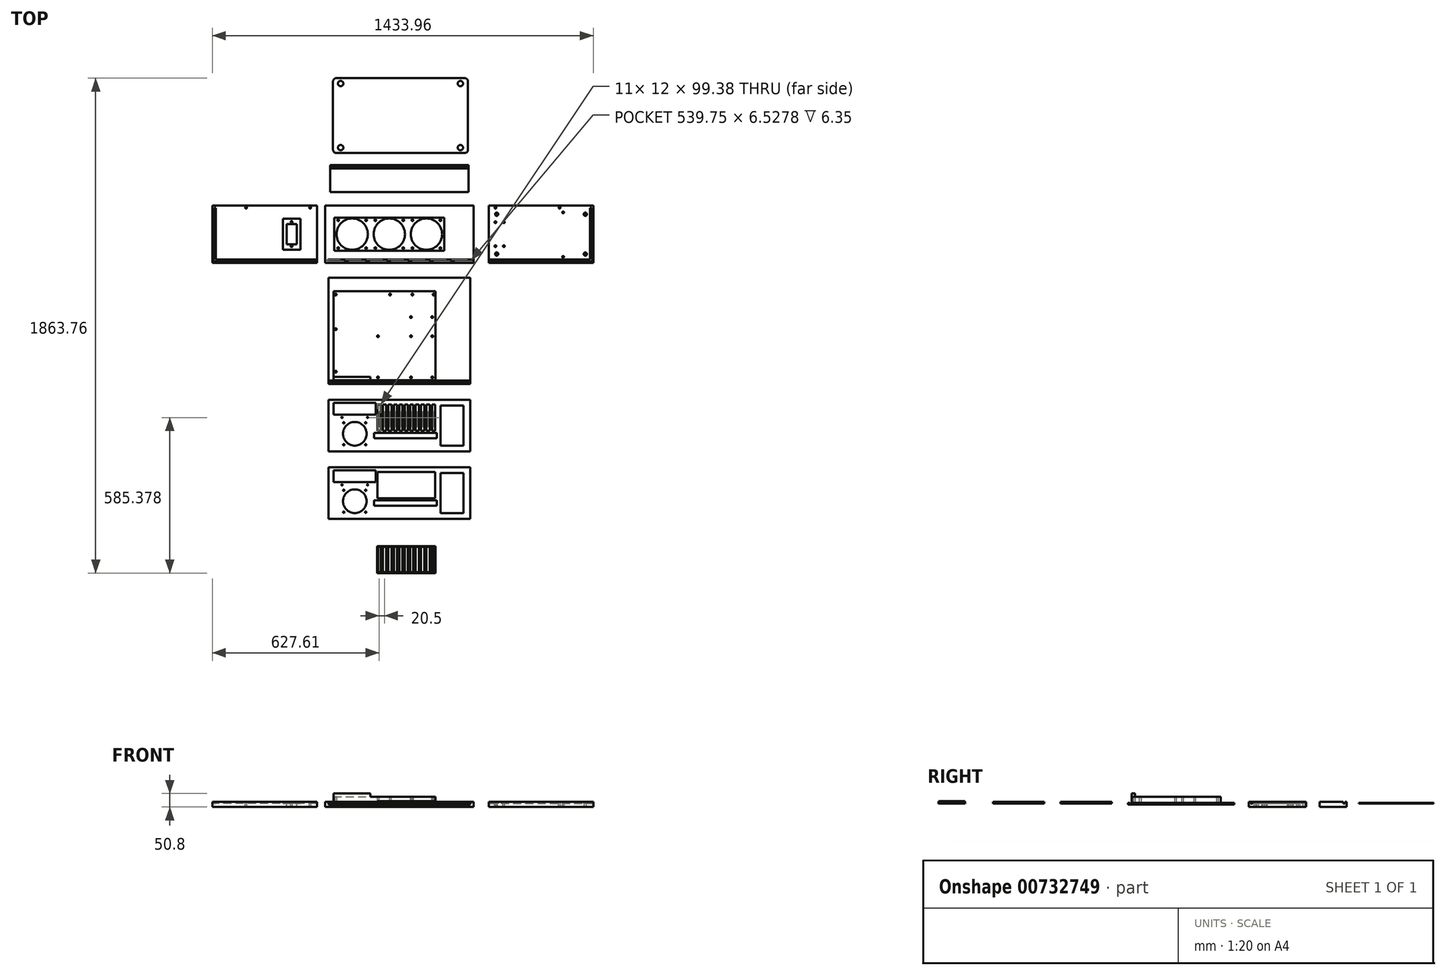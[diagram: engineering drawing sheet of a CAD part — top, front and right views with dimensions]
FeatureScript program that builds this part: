
annotation { "Feature Type Name" : "Feature", "Feature Type Description" : "" }
export const myFeature = defineFeature(function(context is Context, id is Id, definition is map)
    precondition{}
    {
        {
            var Q0;
            Q0=qCreatedBy(makeId("Top.planeOp"),FACE);
            var sketch = newSketch(context, id + "F0", { "sketchPlane" : qUnion([Q0])});
            skLineSegment(sketch, "E0.bottom", {"start": v(279.4, -107.95) * mm, "end": v(-279.4, -107.95) * mm});
            skLineSegment(sketch, "E0.top", {"start": v(279.4, 107.95) * mm, "end": v(-279.4, 107.95) * mm});
            skLineSegment(sketch, "E0.left", {"start": v(279.4, -107.95) * mm, "end": v(279.4, 107.95) * mm});
            skLineSegment(sketch, "E0.right", {"start": v(-279.4, -107.95) * mm, "end": v(-279.4, 107.95) * mm});
            skPoint(sketch, "E0.middle", {"position": v(0, 0) * mm});
            skLineSegment(sketch, "E1.bottom", {"start": v(269.88, -101.6) * mm, "end": v(-269.88, -101.6) * mm});
            skLineSegment(sketch, "E1.top", {"start": v(269.88, -95.07) * mm, "end": v(-269.88, -95.07) * mm});
            skLineSegment(sketch, "E1.left", {"start": v(269.88, -101.6) * mm, "end": v(269.88, -95.07) * mm});
            skLineSegment(sketch, "E1.right", {"start": v(-269.88, -101.6) * mm, "end": v(-269.88, -95.07) * mm});
            skPoint(sketch, "E1.middle", {"position": v(0, -98.34) * mm});
            skCircle(sketch, "E2", {"center": v(101.6, 0) * mm, "radius": 59 * mm});
            skCircle(sketch, "E3", {"center": v(-177.8, 0) * mm, "radius": 59 * mm});
            skCircle(sketch, "E4", {"center": v(-38.1, 0) * mm, "radius": 59 * mm});
            skCircle(sketch, "E5", {"center": v(-230.3, 52.5) * mm, "radius": 3.19 * mm});
            skCircle(sketch, "E6", {"center": v(-230.3, -52.5) * mm, "radius": 3.19 * mm});
            skCircle(sketch, "E7", {"center": v(-125.3, -52.5) * mm, "radius": 3.19 * mm});
            skCircle(sketch, "E8", {"center": v(-125.3, 52.5) * mm, "radius": 3.19 * mm});
            skCircle(sketch, "E9", {"center": v(-90.6, 52.5) * mm, "radius": 3.19 * mm});
            skCircle(sketch, "E10", {"center": v(14.4, 52.5) * mm, "radius": 3.19 * mm});
            skCircle(sketch, "E11", {"center": v(-90.6, -52.5) * mm, "radius": 3.19 * mm});
            skCircle(sketch, "E12", {"center": v(14.4, -52.5) * mm, "radius": 3.19 * mm});
            skCircle(sketch, "E13", {"center": v(49.1, -52.5) * mm, "radius": 3.19 * mm});
            skCircle(sketch, "E14", {"center": v(49.1, 52.5) * mm, "radius": 3.19 * mm});
            skCircle(sketch, "E15", {"center": v(154.1, 52.5) * mm, "radius": 3.19 * mm});
            skCircle(sketch, "E16", {"center": v(154.1, -52.5) * mm, "radius": 3.19 * mm});
            skLineSegment(sketch, "E17.bottom", {"start": v(169.07, -62.5) * mm, "end": v(-245.27, -62.5) * mm});
            skLineSegment(sketch, "E17.top", {"start": v(169.07, 62.5) * mm, "end": v(-245.27, 62.5) * mm});
            skLineSegment(sketch, "E17.left", {"start": v(169.07, -62.5) * mm, "end": v(169.07, 62.5) * mm});
            skLineSegment(sketch, "E17.right", {"start": v(-245.27, -62.5) * mm, "end": v(-245.27, 62.5) * mm});
            skSolve(sketch);
        }
        {
            var Q0;
            Q0=makeQuery(id+"F0.imprint","IMPRINT",FACE,{"disambiguationData":[TD([[makeQuery(id+"F0.imprint","IMPRINT",EDGE,{"derivedFrom":sQuery(id+"F0.wireOp",EDGE,"E1.bottom")}),-1.0]])]});
            var Q1;
            Q1=makeQuery(id+"F0.imprint","IMPRINT",FACE,{"disambiguationData":[TD([[makeQuery(id+"F0.imprint","IMPRINT",EDGE,{"derivedFrom":sQuery(id+"F0.wireOp",EDGE,"E0.bottom")}),-1.0]])]});
            var Q2;
            Q2=makeQuery(id+"F0.imprint","IMPRINT",FACE,{"disambiguationData":[TD([[makeQuery(id+"F0.imprint","IMPRINT",EDGE,{"derivedFrom":sQuery(id+"F0.wireOp",EDGE,"E2")}),-1.0]])]});
            extrude(context, id + "F1", {"entities" : qUnion([Q0, Q1, Q2]), "oppositeDirection" : true, "depth" : 12.7 * mm, "offsetDistance" : 25.4 * mm});
        }
        {
            var Q0;
            Q0=makeQuery(id+"F0.imprint","IMPRINT",FACE,{"disambiguationData":[TD([[makeQuery(id+"F0.imprint","IMPRINT",EDGE,{"derivedFrom":sQuery(id+"F0.wireOp",EDGE,"E0.bottom")}),-1.0]])]});
            extrude(context, id + "F2", {"entities" : qUnion([Q0]), "operationType" : NewBodyOperationType.ADD, "depth" : 6.35 * mm, "offsetDistance" : 25.4 * mm});
        }
        {
            var Q0;
            Q0=qCreatedBy(makeId("Top.planeOp"),FACE);
            var sketch = newSketch(context, id + "F3", { "sketchPlane" : qUnion([Q0])});
            skPoint(sketch, "E18.0", {"position": v(269.88, -95.07) * mm});
            skPoint(sketch, "E18.1", {"position": v(269.88, -101.6) * mm});
            skPoint(sketch, "E18.2", {"position": v(279.4, -107.95) * mm});
            skPoint(sketch, "E18.3", {"position": v(279.4, 107.95) * mm});
            skLineSegment(sketch, "E19.bottom", {"start": v(336.1, -107.95) * mm, "end": v(729.8, -107.95) * mm});
            skLineSegment(sketch, "E19.top", {"start": v(336.1, 107.95) * mm, "end": v(729.8, 107.95) * mm});
            skLineSegment(sketch, "E19.left", {"start": v(336.1, -107.95) * mm, "end": v(336.1, 107.95) * mm});
            skLineSegment(sketch, "E19.right", {"start": v(729.8, -107.95) * mm, "end": v(729.8, 107.95) * mm});
            skPoint(sketch, "E19.middle", {"position": v(532.95, 0) * mm});
            skLineSegment(sketch, "E20.bottom", {"start": v(332.93, -95.07) * mm, "end": v(732.98, -95.07) * mm});
            skLineSegment(sketch, "E20.top", {"start": v(332.93, -101.6) * mm, "end": v(732.98, -101.6) * mm});
            skLineSegment(sketch, "E20.left", {"start": v(332.93, -95.07) * mm, "end": v(332.93, -101.6) * mm});
            skLineSegment(sketch, "E20.right", {"start": v(732.98, -95.07) * mm, "end": v(732.98, -101.6) * mm});
            skLineSegment(sketch, "E21.bottom", {"start": v(723.45, -97.9) * mm, "end": v(717.08, -97.9) * mm});
            skLineSegment(sketch, "E21.top", {"start": v(723.45, 98.42) * mm, "end": v(717.08, 98.42) * mm});
            skLineSegment(sketch, "E21.left", {"start": v(723.45, -97.9) * mm, "end": v(723.45, 98.42) * mm});
            skLineSegment(sketch, "E21.right", {"start": v(717.08, -97.9) * mm, "end": v(717.08, 98.42) * mm});
            skCircle(sketch, "E22", {"center": v(366.1, 74.95) * mm, "radius": 3.3 * mm});
            skCircle(sketch, "E23", {"center": v(366.1, -74.95) * mm, "radius": 3.3 * mm});
            skCircle(sketch, "E24", {"center": v(699.8, -74.95) * mm, "radius": 3.3 * mm});
            skCircle(sketch, "E25", {"center": v(699.8, 74.95) * mm, "radius": 3.3 * mm});
            skCircle(sketch, "E26", {"center": v(366.1, 74.95) * mm, "radius": 6 * mm});
            skCircle(sketch, "E27", {"center": v(366.1, -74.95) * mm, "radius": 6 * mm});
            skCircle(sketch, "E28", {"center": v(699.8, 74.95) * mm, "radius": 6 * mm});
            skCircle(sketch, "E29", {"center": v(699.8, -74.95) * mm, "radius": 6 * mm});
            skPoint(sketch, "E30", {"position": v(628.2, -20.34) * mm});
            skCircle(sketch, "E31", {"center": v(602.8, 99.95) * mm, "radius": 3.3 * mm});
            skCircle(sketch, "E32", {"center": v(361.5, 99.95) * mm, "radius": 3.3 * mm});
            skPoint(sketch, "E33.centerSnap0", {"position": v(336.1, 0) * mm});
            skCircle(sketch, "E34", {"center": v(616.08, 81.95) * mm, "radius": 3.3 * mm});
            skCircle(sketch, "E35", {"center": v(616.08, -85.4) * mm, "radius": 3.3 * mm});
            skLineSegment(sketch, "E36.bottom", {"start": v(393.3, -45.09) * mm, "end": v(361.5, -45.09) * mm});
            skLineSegment(sketch, "E36.top", {"start": v(393.3, 45.08) * mm, "end": v(361.5, 45.08) * mm});
            skLineSegment(sketch, "E36.left", {"start": v(393.3, -45.09) * mm, "end": v(393.3, 45.08) * mm});
            skLineSegment(sketch, "E36.right", {"start": v(361.5, -45.09) * mm, "end": v(361.5, 45.08) * mm});
            skPoint(sketch, "E36.middle", {"position": v(377.4, 0) * mm});
            skCircle(sketch, "E37", {"center": v(361.5, 45.08) * mm, "radius": 3.3 * mm});
            skCircle(sketch, "E38", {"center": v(393.3, 45.08) * mm, "radius": 3.3 * mm});
            skCircle(sketch, "E39", {"center": v(361.5, -45.09) * mm, "radius": 3.3 * mm});
            skCircle(sketch, "E40", {"center": v(393.3, -45.09) * mm, "radius": 3.3 * mm});
            skSolve(sketch);
        }
        {
            var Q0;
            {var subQ0=sQuery(id+"F3.wireOp",EDGE,"E19.left");var subQ1=sQuery(id+"F3.wireOp",EDGE,"E19.top");var subQ2=makeQuery(id+"F3.imprint","INTERSECT",VERTEX,{"derivedFrom":[subQ1,subQ0]});Q0=makeQuery(id+"F3.imprint","IMPRINT",FACE,{"disambiguationData":[TD([[makeQuery(id+"F3.imprint","IMPRINT",EDGE,{"disambiguationData":[TD([[subQ2,-1.0]])],"derivedFrom":subQ1}),-1.0]])]});}
            var Q1;
            {var subQ0=sQuery(id+"F3.wireOp",EDGE,"E21.right");var subQ1=sQuery(id+"F3.wireOp",EDGE,"E19.top");var subQ2=makeQuery(id+"F3.imprint","INTERSECT",VERTEX,{"derivedFrom":[subQ1,subQ0]});Q1=makeQuery(id+"F3.imprint","IMPRINT",FACE,{"disambiguationData":[TD([[makeQuery(id+"F3.imprint","IMPRINT",EDGE,{"disambiguationData":[TD([[subQ2,-1.0]])],"derivedFrom":subQ1}),-1.0]])]});}
            var Q2;
            {var subQ0=sQuery(id+"F3.wireOp",EDGE,"E19.right");var subQ1=sQuery(id+"F3.wireOp",EDGE,"E19.top");var subQ2=makeQuery(id+"F3.imprint","INTERSECT",VERTEX,{"derivedFrom":[subQ1,subQ0]});Q2=makeQuery(id+"F3.imprint","IMPRINT",FACE,{"disambiguationData":[TD([[makeQuery(id+"F3.imprint","IMPRINT",EDGE,{"disambiguationData":[TD([[subQ2,1.0]])],"derivedFrom":subQ1}),-1.0]])]});}
            var Q3;
            {var subQ6=sQuery(id+"F3.wireOp",EDGE,"E21.bottom");Q3=makeQuery(id+"F3.imprint","IMPRINT",FACE,{"disambiguationData":[TD([[makeQuery(id+"F3.imprint","IMPRINT",EDGE,{"derivedFrom":subQ6}),1.0]])]});}
            var Q4;
            {var subQ0=sQuery(id+"F3.wireOp",EDGE,"E19.bottom");Q4=makeQuery(id+"F3.imprint","IMPRINT",FACE,{"disambiguationData":[TD([[makeQuery(id+"F3.imprint","IMPRINT",EDGE,{"derivedFrom":subQ0}),1.0]])]});}
            var Q5;
            {var subQ5=sQuery(id+"F3.wireOp",EDGE,"E21.bottom");Q5=makeQuery(id+"F3.imprint","IMPRINT",FACE,{"disambiguationData":[TD([[makeQuery(id+"F3.imprint","IMPRINT",EDGE,{"derivedFrom":subQ5}),-1.0]])]});}
            var Q6;
            {var subQ5=sQuery(id+"F3.wireOp",EDGE,"E21.top");Q6=makeQuery(id+"F3.imprint","IMPRINT",FACE,{"disambiguationData":[TD([[makeQuery(id+"F3.imprint","IMPRINT",EDGE,{"derivedFrom":subQ5}),1.0]])]});}
            var Q7;
            Q7=makeQuery(id+"F3.imprint","IMPRINT",FACE,{"disambiguationData":[TD([[makeQuery(id+"F3.imprint","IMPRINT",EDGE,{"derivedFrom":sQuery(id+"F3.wireOp",EDGE,"E22")}),-1.0]])]});
            var Q8;
            Q8=makeQuery(id+"F3.imprint","IMPRINT",FACE,{"disambiguationData":[TD([[makeQuery(id+"F3.imprint","IMPRINT",EDGE,{"derivedFrom":sQuery(id+"F3.wireOp",EDGE,"E23")}),-1.0]])]});
            var Q9;
            Q9=makeQuery(id+"F3.imprint","IMPRINT",FACE,{"disambiguationData":[TD([[makeQuery(id+"F3.imprint","IMPRINT",EDGE,{"derivedFrom":sQuery(id+"F3.wireOp",EDGE,"E24")}),-1.0]])]});
            var Q10;
            Q10=makeQuery(id+"F3.imprint","IMPRINT",FACE,{"disambiguationData":[TD([[makeQuery(id+"F3.imprint","IMPRINT",EDGE,{"derivedFrom":sQuery(id+"F3.wireOp",EDGE,"E25")}),-1.0]])]});
            var Q11;
            {var subQ0=sQuery(id+"F3.wireOp",EDGE,"E36.top");var subQ1=sQuery(id+"F3.wireOp",EDGE,"oCOWhfAx-kF6R-myvc-yPfL-ItVIfWdrZVwj");var subQ2=makeQuery(id+"F3.imprint","INTERSECT",VERTEX,{"derivedFrom":[subQ1,subQ0]});Q11=makeQuery(id+"F3.imprint","IMPRINT",FACE,{"disambiguationData":[TD([[makeQuery(id+"F3.imprint","IMPRINT",EDGE,{"disambiguationData":[TD([[subQ2,-1.0]])],"derivedFrom":subQ1}),-1.0]])]});}
            var Q12;
            {var subQ5=sQuery(id+"F3.wireOp",EDGE,"E36.top");var subQ6=sQuery(id+"F3.wireOp",EDGE,"oCOWhfAx-kF6R-myvc-yPfL-ItVIfWdrZVwj");var subQ7=makeQuery(id+"F3.imprint","INTERSECT",VERTEX,{"derivedFrom":[subQ6,subQ5]});Q12=makeQuery(id+"F3.imprint","IMPRINT",FACE,{"disambiguationData":[TD([[makeQuery(id+"F3.imprint","IMPRINT",EDGE,{"disambiguationData":[TD([[subQ7,-1.0]])],"derivedFrom":subQ6}),1.0]])]});}
            var Q13;
            {var subQ5=sQuery(id+"F3.wireOp",EDGE,"E40");var subQ10=sQuery(id+"F3.wireOp",EDGE,"E36.bottom");var subQ11=makeQuery(id+"F3.imprint","INTERSECT",VERTEX,{"derivedFrom":[subQ10,subQ5]});Q13=makeQuery(id+"F3.imprint","IMPRINT",FACE,{"disambiguationData":[TD([[makeQuery(id+"F3.imprint","IMPRINT",EDGE,{"disambiguationData":[TD([[subQ11,-1.0]])],"derivedFrom":subQ10}),-1.0]])]});}
            extrude(context, id + "F4", {"entities" : qUnion([Q0, Q1, Q2, Q3, Q4, Q5, Q6, Q7, Q8, Q9, Q10, Q11, Q12, Q13]), "oppositeDirection" : true, "depth" : 12.7 * mm, "offsetDistance" : 25.4 * mm});
        }
        {
            var Q0;
            {var subQ0=sQuery(id+"F3.wireOp",EDGE,"E19.left");var subQ1=sQuery(id+"F3.wireOp",EDGE,"E19.top");var subQ2=makeQuery(id+"F3.imprint","INTERSECT",VERTEX,{"derivedFrom":[subQ1,subQ0]});Q0=makeQuery(id+"F3.imprint","IMPRINT",FACE,{"disambiguationData":[TD([[makeQuery(id+"F3.imprint","IMPRINT",EDGE,{"disambiguationData":[TD([[subQ2,-1.0]])],"derivedFrom":subQ1}),-1.0]])]});}
            var Q1;
            {var subQ0=sQuery(id+"F3.wireOp",EDGE,"E19.right");var subQ1=sQuery(id+"F3.wireOp",EDGE,"E19.top");var subQ2=makeQuery(id+"F3.imprint","INTERSECT",VERTEX,{"derivedFrom":[subQ1,subQ0]});Q1=makeQuery(id+"F3.imprint","IMPRINT",FACE,{"disambiguationData":[TD([[makeQuery(id+"F3.imprint","IMPRINT",EDGE,{"disambiguationData":[TD([[subQ2,1.0]])],"derivedFrom":subQ1}),-1.0]])]});}
            var Q2;
            {var subQ0=sQuery(id+"F3.wireOp",EDGE,"E19.bottom");Q2=makeQuery(id+"F3.imprint","IMPRINT",FACE,{"disambiguationData":[TD([[makeQuery(id+"F3.imprint","IMPRINT",EDGE,{"derivedFrom":subQ0}),1.0]])]});}
            var Q3;
            {var subQ0=sQuery(id+"F3.wireOp",EDGE,"E36.top");var subQ1=sQuery(id+"F3.wireOp",EDGE,"oCOWhfAx-kF6R-myvc-yPfL-ItVIfWdrZVwj");var subQ2=makeQuery(id+"F3.imprint","INTERSECT",VERTEX,{"derivedFrom":[subQ1,subQ0]});Q3=makeQuery(id+"F3.imprint","IMPRINT",FACE,{"disambiguationData":[TD([[makeQuery(id+"F3.imprint","IMPRINT",EDGE,{"disambiguationData":[TD([[subQ2,-1.0]])],"derivedFrom":subQ1}),-1.0]])]});}
            var Q4;
            {var subQ5=sQuery(id+"F3.wireOp",EDGE,"E36.top");var subQ6=sQuery(id+"F3.wireOp",EDGE,"oCOWhfAx-kF6R-myvc-yPfL-ItVIfWdrZVwj");var subQ7=makeQuery(id+"F3.imprint","INTERSECT",VERTEX,{"derivedFrom":[subQ6,subQ5]});Q4=makeQuery(id+"F3.imprint","IMPRINT",FACE,{"disambiguationData":[TD([[makeQuery(id+"F3.imprint","IMPRINT",EDGE,{"disambiguationData":[TD([[subQ7,-1.0]])],"derivedFrom":subQ6}),1.0]])]});}
            var Q5;
            {var subQ5=sQuery(id+"F3.wireOp",EDGE,"E40");var subQ10=sQuery(id+"F3.wireOp",EDGE,"E36.bottom");var subQ11=makeQuery(id+"F3.imprint","INTERSECT",VERTEX,{"derivedFrom":[subQ10,subQ5]});Q5=makeQuery(id+"F3.imprint","IMPRINT",FACE,{"disambiguationData":[TD([[makeQuery(id+"F3.imprint","IMPRINT",EDGE,{"disambiguationData":[TD([[subQ11,-1.0]])],"derivedFrom":subQ10}),-1.0]])]});}
            extrude(context, id + "F5", {"entities" : qUnion([Q0, Q1, Q2, Q3, Q4, Q5]), "operationType" : NewBodyOperationType.ADD, "depth" : 6.35 * mm, "offsetDistance" : 25.4 * mm});
        }
        {
            var Q0;
            Q0=qCreatedBy(makeId("Top.planeOp"),FACE);
            var sketch = newSketch(context, id + "F6", { "sketchPlane" : qUnion([Q0])});
            skPoint(sketch, "E41.0", {"position": v(-279.4, 107.95) * mm});
            skPoint(sketch, "E41.1", {"position": v(-279.4, -107.95) * mm});
            skPoint(sketch, "E41.2", {"position": v(-269.88, -95.07) * mm});
            skPoint(sketch, "E41.3", {"position": v(-269.88, -101.6) * mm});
            skLineSegment(sketch, "E42.bottom", {"start": v(-310.46, 107.95) * mm, "end": v(-704.16, 107.95) * mm});
            skLineSegment(sketch, "E42.top", {"start": v(-310.46, -107.95) * mm, "end": v(-704.16, -107.95) * mm});
            skLineSegment(sketch, "E42.left", {"start": v(-310.46, 107.95) * mm, "end": v(-310.46, -107.95) * mm});
            skLineSegment(sketch, "E42.right", {"start": v(-704.16, 107.95) * mm, "end": v(-704.16, -107.95) * mm});
            skLineSegment(sketch, "E43.bottom", {"start": v(-307.28, -95.07) * mm, "end": v(-707.33, -95.07) * mm});
            skLineSegment(sketch, "E43.top", {"start": v(-307.28, -101.6) * mm, "end": v(-707.33, -101.6) * mm});
            skLineSegment(sketch, "E43.left", {"start": v(-307.28, -95.07) * mm, "end": v(-307.28, -101.6) * mm});
            skLineSegment(sketch, "E43.right", {"start": v(-707.33, -95.07) * mm, "end": v(-707.33, -101.6) * mm});
            skLineSegment(sketch, "E44.bottom", {"start": v(-386.66, -38.1) * mm, "end": v(-424.76, -38.1) * mm});
            skLineSegment(sketch, "E44.top", {"start": v(-386.66, 38.1) * mm, "end": v(-424.76, 38.1) * mm});
            skLineSegment(sketch, "E44.left", {"start": v(-386.66, -38.1) * mm, "end": v(-386.66, 38.1) * mm});
            skLineSegment(sketch, "E44.right", {"start": v(-424.76, -38.1) * mm, "end": v(-424.76, 38.1) * mm});
            skPoint(sketch, "E44.middle", {"position": v(-405.7, 0) * mm});
            skLineSegment(sketch, "E45.bottom", {"start": v(-697.8, 98.42) * mm, "end": v(-691.43, 98.42) * mm});
            skLineSegment(sketch, "E45.top", {"start": v(-697.8, -99.05) * mm, "end": v(-691.43, -99.05) * mm});
            skLineSegment(sketch, "E45.left", {"start": v(-697.8, 98.42) * mm, "end": v(-697.8, -99.05) * mm});
            skLineSegment(sketch, "E45.right", {"start": v(-691.43, 98.42) * mm, "end": v(-691.43, -99.05) * mm});
            skPoint(sketch, "E46.0", {"position": v(361.5, 99.95) * mm});
            skCircle(sketch, "E47", {"center": v(-335.86, 99.95) * mm, "radius": 3.3 * mm});
            skCircle(sketch, "E48", {"center": v(-577.16, 99.95) * mm, "radius": 3.3 * mm});
            skCircle(sketch, "E49", {"center": v(-405.7, 45.6) * mm, "radius": 3.3 * mm});
            skCircle(sketch, "E50", {"center": v(-405.7, -45.6) * mm, "radius": 3.3 * mm});
            skLineSegment(sketch, "E51.bottom", {"start": v(-438.73, 58.42) * mm, "end": v(-372.69, 58.42) * mm});
            skLineSegment(sketch, "E51.top", {"start": v(-438.73, -58.42) * mm, "end": v(-372.69, -58.42) * mm});
            skLineSegment(sketch, "E51.left", {"start": v(-438.73, 58.42) * mm, "end": v(-438.73, -58.42) * mm});
            skLineSegment(sketch, "E51.right", {"start": v(-372.69, 58.42) * mm, "end": v(-372.69, -58.42) * mm});
            skSolve(sketch);
        }
        {
            var Q0;
            Q0=makeQuery(id+"F6.imprint","IMPRINT",FACE,{"disambiguationData":[TD([[makeQuery(id+"F6.imprint","IMPRINT",EDGE,{"derivedFrom":sQuery(id+"F6.wireOp",EDGE,"E44.bottom")}),1.0]])]});
            var Q1;
            {var subQ0=sQuery(id+"F6.wireOp",EDGE,"E42.top");Q1=makeQuery(id+"F6.imprint","IMPRINT",FACE,{"disambiguationData":[TD([[makeQuery(id+"F6.imprint","IMPRINT",EDGE,{"derivedFrom":subQ0}),-1.0]])]});}
            var Q2;
            {var subQ12=sQuery(id+"F6.wireOp",EDGE,"E45.top");Q2=makeQuery(id+"F6.imprint","IMPRINT",FACE,{"disambiguationData":[TD([[makeQuery(id+"F6.imprint","IMPRINT",EDGE,{"derivedFrom":subQ12}),-1.0]])]});}
            var Q3;
            {var subQ0=sQuery(id+"F6.wireOp",EDGE,"E42.right");var subQ1=sQuery(id+"F6.wireOp",EDGE,"E42.bottom");var subQ2=makeQuery(id+"F6.imprint","INTERSECT",VERTEX,{"derivedFrom":[subQ1,subQ0]});Q3=makeQuery(id+"F6.imprint","IMPRINT",FACE,{"disambiguationData":[TD([[makeQuery(id+"F6.imprint","IMPRINT",EDGE,{"disambiguationData":[TD([[subQ2,1.0]])],"derivedFrom":subQ1}),1.0]])]});}
            var Q4;
            {var subQ0=sQuery(id+"F6.wireOp",EDGE,"E45.right");var subQ1=sQuery(id+"F6.wireOp",EDGE,"E42.bottom");var subQ2=makeQuery(id+"F6.imprint","INTERSECT",VERTEX,{"derivedFrom":[subQ1,subQ0]});Q4=makeQuery(id+"F6.imprint","IMPRINT",FACE,{"disambiguationData":[TD([[makeQuery(id+"F6.imprint","IMPRINT",EDGE,{"disambiguationData":[TD([[subQ2,-1.0]])],"derivedFrom":subQ1}),1.0]])]});}
            var Q5;
            {var subQ5=sQuery(id+"F6.wireOp",EDGE,"E45.top");Q5=makeQuery(id+"F6.imprint","IMPRINT",FACE,{"disambiguationData":[TD([[makeQuery(id+"F6.imprint","IMPRINT",EDGE,{"derivedFrom":subQ5}),1.0]])]});}
            var Q6;
            {var subQ5=sQuery(id+"F6.wireOp",EDGE,"E45.bottom");Q6=makeQuery(id+"F6.imprint","IMPRINT",FACE,{"disambiguationData":[TD([[makeQuery(id+"F6.imprint","IMPRINT",EDGE,{"derivedFrom":subQ5}),-1.0]])]});}
            extrude(context, id + "F7", {"entities" : qUnion([Q0, Q1, Q2, Q3, Q4, Q5, Q6]), "oppositeDirection" : true, "depth" : 12.7 * mm, "offsetDistance" : 25.4 * mm});
        }
        {
            var Q0;
            Q0=makeQuery(id+"F6.imprint","IMPRINT",FACE,{"disambiguationData":[TD([[makeQuery(id+"F6.imprint","IMPRINT",EDGE,{"derivedFrom":sQuery(id+"F6.wireOp",EDGE,"E44.bottom")}),1.0]])]});
            var Q1;
            {var subQ0=sQuery(id+"F6.wireOp",EDGE,"E42.right");var subQ1=sQuery(id+"F6.wireOp",EDGE,"E42.bottom");var subQ2=makeQuery(id+"F6.imprint","INTERSECT",VERTEX,{"derivedFrom":[subQ1,subQ0]});Q1=makeQuery(id+"F6.imprint","IMPRINT",FACE,{"disambiguationData":[TD([[makeQuery(id+"F6.imprint","IMPRINT",EDGE,{"disambiguationData":[TD([[subQ2,1.0]])],"derivedFrom":subQ1}),1.0]])]});}
            var Q2;
            {var subQ0=sQuery(id+"F6.wireOp",EDGE,"E42.top");Q2=makeQuery(id+"F6.imprint","IMPRINT",FACE,{"disambiguationData":[TD([[makeQuery(id+"F6.imprint","IMPRINT",EDGE,{"derivedFrom":subQ0}),-1.0]])]});}
            extrude(context, id + "F8", {"entities" : qUnion([Q0, Q1, Q2]), "operationType" : NewBodyOperationType.ADD, "depth" : 6.35 * mm, "offsetDistance" : 25.4 * mm});
        }
        {
            var Q0;
            Q0=makeQuery(id+"F6.imprint","IMPRINT",FACE,{"disambiguationData":[TD([[makeQuery(id+"F6.imprint","IMPRINT",EDGE,{"derivedFrom":sQuery(id+"F6.wireOp",EDGE,"E44.bottom")}),1.0]])]});
            extrude(context, id + "F9", {"entities" : qUnion([Q0]), "operationType" : NewBodyOperationType.REMOVE, "depth" : 6.35 * mm, "offsetDistance" : 25.4 * mm});
        }
        {
            var Q0;
            Q0=qCreatedBy(makeId("Top.planeOp"),FACE);
            var sketch = newSketch(context, id + "F10", { "sketchPlane" : qUnion([Q0])});
            skLineSegment(sketch, "E52.bottom", {"start": v(136.35, -214.45) * mm, "end": v(136.35, -549.45) * mm});
            skLineSegment(sketch, "E52.top", {"start": v(-247.65, -214.45) * mm, "end": v(-247.65, -549.45) * mm});
            skLineSegment(sketch, "E52.left", {"start": v(136.35, -214.45) * mm, "end": v(-247.65, -214.45) * mm});
            skLineSegment(sketch, "E52.right", {"start": v(136.35, -549.45) * mm, "end": v(-247.65, -549.45) * mm});
            skLineSegment(sketch, "E53.bottom", {"start": v(-109.56, -549.45) * mm, "end": v(-109.56, -536.83) * mm});
            skLineSegment(sketch, "E53.top", {"start": v(-247.65, -549.45) * mm, "end": v(-247.65, -536.83) * mm});
            skLineSegment(sketch, "E53.left", {"start": v(-109.56, -549.45) * mm, "end": v(-247.65, -549.45) * mm});
            skLineSegment(sketch, "E53.right", {"start": v(-109.56, -536.83) * mm, "end": v(-247.65, -536.83) * mm});
            skCircle(sketch, "E54", {"center": v(-239.65, -517.45) * mm, "radius": 3.3 * mm});
            skCircle(sketch, "E55", {"center": v(-239.65, -357.45) * mm, "radius": 3.3 * mm});
            skCircle(sketch, "E56", {"center": v(-239.65, -227.45) * mm, "radius": 3.3 * mm});
            skCircle(sketch, "E57", {"center": v(-80.65, -539.45) * mm, "radius": 3.3 * mm});
            skCircle(sketch, "E58", {"center": v(-80.65, -384.45) * mm, "radius": 3.3 * mm});
            skCircle(sketch, "E59", {"center": v(43.35, -539.45) * mm, "radius": 3.3 * mm});
            skCircle(sketch, "E60", {"center": v(123.35, -539.45) * mm, "radius": 3.3 * mm});
            skCircle(sketch, "E61", {"center": v(123.35, -384.45) * mm, "radius": 3.3 * mm});
            skCircle(sketch, "E62", {"center": v(43.35, -384.45) * mm, "radius": 3.3 * mm});
            skCircle(sketch, "E63", {"center": v(123.35, -312.45) * mm, "radius": 3.3 * mm});
            skCircle(sketch, "E64", {"center": v(43.35, -312.45) * mm, "radius": 3.3 * mm});
            skCircle(sketch, "E65", {"center": v(128.85, -227.45) * mm, "radius": 3.3 * mm});
            skCircle(sketch, "E66", {"center": v(48.85, -227.45) * mm, "radius": 3.3 * mm});
            skCircle(sketch, "E67", {"center": v(-35.15, -227.45) * mm, "radius": 3.3 * mm});
            skSolve(sketch);
        }
        {
            var Q0;
            Q0=makeQuery(id+"F10.imprint","IMPRINT",FACE,{"disambiguationData":[TD([[makeQuery(id+"F10.imprint","IMPRINT",EDGE,{"derivedFrom":sQuery(id+"F10.wireOp",EDGE,"E52.bottom")}),-1.0]])]});
            var Q1;
            Q1=makeQuery(id+"F10.imprint","IMPRINT",FACE,{"disambiguationData":[TD([[makeQuery(id+"F10.imprint","IMPRINT",EDGE,{"derivedFrom":sQuery(id+"F10.wireOp",EDGE,"E53.bottom")}),1.0]])]});
            extrude(context, id + "F11", {"entities" : qUnion([Q0, Q1]), "depth" : 25.4 * mm, "offsetDistance" : 25.4 * mm});
        }
        {
            var Q0;
            Q0=makeQuery(id+"F10.imprint","IMPRINT",FACE,{"disambiguationData":[TD([[makeQuery(id+"F10.imprint","IMPRINT",EDGE,{"derivedFrom":sQuery(id+"F10.wireOp",EDGE,"E53.bottom")}),1.0]])]});
            extrude(context, id + "F12", {"entities" : qUnion([Q0]), "operationType" : NewBodyOperationType.ADD, "depth" : 38.1 * mm, "offsetDistance" : 25.4 * mm});
        }
        {
            var Q0;
            Q0=qCreatedBy(makeId("Top.planeOp"),FACE);
            var sketch = newSketch(context, id + "F13", { "sketchPlane" : qUnion([Q0])});
            skLineSegment(sketch, "E68.bottom", {"start": v(266.7, -563.67) * mm, "end": v(-266.7, -563.67) * mm});
            skLineSegment(sketch, "E68.top", {"start": v(266.7, -163.62) * mm, "end": v(-266.7, -163.62) * mm});
            skLineSegment(sketch, "E68.left", {"start": v(266.7, -563.67) * mm, "end": v(266.7, -163.62) * mm});
            skLineSegment(sketch, "E68.right", {"start": v(-266.7, -563.67) * mm, "end": v(-266.7, -163.62) * mm});
            skPoint(sketch, "E69.0", {"position": v(-279.4, -107.95) * mm});
            skPoint(sketch, "E69.1", {"position": v(279.4, -107.95) * mm});
            skLineSegment(sketch, "E70.bottom", {"start": v(269.88, -557.32) * mm, "end": v(-269.88, -557.32) * mm});
            skLineSegment(sketch, "E70.top", {"start": v(269.88, -550.8) * mm, "end": v(-269.88, -550.8) * mm});
            skLineSegment(sketch, "E70.left", {"start": v(269.88, -557.32) * mm, "end": v(269.88, -550.8) * mm});
            skLineSegment(sketch, "E70.right", {"start": v(-269.88, -557.32) * mm, "end": v(-269.88, -550.8) * mm});
            skCircle(sketch, "E71.0", {"center": v(-239.65, -227.45) * mm, "radius": 3.3 * mm});
            skCircle(sketch, "E71.1", {"center": v(-35.15, -227.45) * mm, "radius": 3.3 * mm});
            skCircle(sketch, "E71.2", {"center": v(48.85, -227.45) * mm, "radius": 3.3 * mm});
            skCircle(sketch, "E71.3", {"center": v(128.85, -227.45) * mm, "radius": 3.3 * mm});
            skCircle(sketch, "E71.4", {"center": v(43.35, -312.45) * mm, "radius": 3.3 * mm});
            skCircle(sketch, "E71.5", {"center": v(123.35, -312.45) * mm, "radius": 3.3 * mm});
            skCircle(sketch, "E71.6", {"center": v(43.35, -384.45) * mm, "radius": 3.3 * mm});
            skCircle(sketch, "E71.7", {"center": v(-80.65, -384.45) * mm, "radius": 3.3 * mm});
            skCircle(sketch, "E71.8", {"center": v(123.35, -384.45) * mm, "radius": 3.3 * mm});
            skCircle(sketch, "E71.9", {"center": v(-239.65, -357.45) * mm, "radius": 3.3 * mm});
            skCircle(sketch, "E71.10", {"center": v(-239.65, -517.45) * mm, "radius": 3.3 * mm});
            skCircle(sketch, "E71.11", {"center": v(-80.65, -539.45) * mm, "radius": 3.3 * mm});
            skCircle(sketch, "E71.12", {"center": v(43.35, -539.45) * mm, "radius": 3.3 * mm});
            skCircle(sketch, "E71.13", {"center": v(123.35, -539.45) * mm, "radius": 3.3 * mm});
            skSolve(sketch);
        }
        {
            var Q0;
            {var subQ0=sQuery(id+"F13.wireOp",EDGE,"E68.top");Q0=makeQuery(id+"F13.imprint","IMPRINT",FACE,{"disambiguationData":[TD([[makeQuery(id+"F13.imprint","IMPRINT",EDGE,{"derivedFrom":subQ0}),1.0]])]});}
            var Q1;
            {var subQ0=sQuery(id+"F13.wireOp",EDGE,"E70.bottom");var subQ1=sQuery(id+"F13.wireOp",EDGE,"E68.left");var subQ2=makeQuery(id+"F13.imprint","INTERSECT",VERTEX,{"derivedFrom":[subQ1,subQ0]});Q1=makeQuery(id+"F13.imprint","IMPRINT",FACE,{"disambiguationData":[TD([[makeQuery(id+"F13.imprint","IMPRINT",EDGE,{"disambiguationData":[TD([[subQ2,-1.0]])],"derivedFrom":subQ1}),1.0]])]});}
            var Q2;
            {var subQ0=sQuery(id+"F13.wireOp",EDGE,"E68.bottom");Q2=makeQuery(id+"F13.imprint","IMPRINT",FACE,{"disambiguationData":[TD([[makeQuery(id+"F13.imprint","IMPRINT",EDGE,{"derivedFrom":subQ0}),-1.0]])]});}
            extrude(context, id + "F14", {"entities" : qUnion([Q0, Q1, Q2]), "oppositeDirection" : true, "depth" : 3.2 * mm, "offsetDistance" : 25.4 * mm});
        }
        {
            var Q0;
            {var subQ0=sQuery(id+"F13.wireOp",EDGE,"E68.top");Q0=makeQuery(id+"F13.imprint","IMPRINT",FACE,{"disambiguationData":[TD([[makeQuery(id+"F13.imprint","IMPRINT",EDGE,{"derivedFrom":subQ0}),1.0]])]});}
            var Q1;
            {var subQ0=sQuery(id+"F13.wireOp",EDGE,"E68.bottom");Q1=makeQuery(id+"F13.imprint","IMPRINT",FACE,{"disambiguationData":[TD([[makeQuery(id+"F13.imprint","IMPRINT",EDGE,{"derivedFrom":subQ0}),-1.0]])]});}
            extrude(context, id + "F15", {"entities" : qUnion([Q0, Q1]), "operationType" : NewBodyOperationType.ADD, "depth" : 3.2 * mm, "offsetDistance" : 25.4 * mm});
        }
        {
            var Q0;
            Q0=qCreatedBy(makeId("Top.planeOp"),FACE);
            var sketch = newSketch(context, id + "F16", { "sketchPlane" : qUnion([Q0])});
            skPoint(sketch, "E72.0", {"position": v(-266.7, -563.67) * mm});
            skPoint(sketch, "E72.1", {"position": v(266.7, -563.67) * mm});
            skLineSegment(sketch, "E73.MirrorCS", {"start": v(-9.05, -641.22) * mm, "end": v(-21.05, -641.22) * mm});
            skLineSegment(sketch, "E74.MirrorCS", {"start": v(-29.55, -641.22) * mm, "end": v(-41.55, -641.22) * mm});
            skLineSegment(sketch, "E75.MirrorCS", {"start": v(113.95, -641.22) * mm, "end": v(101.95, -641.22) * mm});
            skLineSegment(sketch, "E76.MirrorCS", {"start": v(72.95, -641.22) * mm, "end": v(60.95, -641.22) * mm});
            skLineSegment(sketch, "E77.MirrorCS", {"start": v(134.45, -740.6) * mm, "end": v(122.45, -740.6) * mm});
            skLineSegment(sketch, "E78.MirrorCS", {"start": v(31.95, -641.22) * mm, "end": v(19.95, -641.22) * mm});
            skLineSegment(sketch, "E79.MirrorCS", {"start": v(-50.05, -641.22) * mm, "end": v(-62.05, -641.22) * mm});
            skLineSegment(sketch, "E80.MirrorCS", {"start": v(113.95, -740.6) * mm, "end": v(101.95, -740.6) * mm});
            skLineSegment(sketch, "E81.MirrorCS", {"start": v(11.45, -641.22) * mm, "end": v(-0.55, -641.22) * mm});
            skLineSegment(sketch, "E82.MirrorCS", {"start": v(-9.05, -740.6) * mm, "end": v(-21.05, -740.6) * mm});
            skLineSegment(sketch, "E83.MirrorCS", {"start": v(52.45, -740.6) * mm, "end": v(40.45, -740.6) * mm});
            skLineSegment(sketch, "E84.MirrorCS", {"start": v(-29.55, -740.6) * mm, "end": v(-41.55, -740.6) * mm});
            skLineSegment(sketch, "E85.MirrorCS", {"start": v(93.45, -641.22) * mm, "end": v(81.45, -641.22) * mm});
            skLineSegment(sketch, "E86.MirrorCS", {"start": v(93.45, -740.6) * mm, "end": v(81.45, -740.6) * mm});
            skLineSegment(sketch, "E87.MirrorCS", {"start": v(11.45, -740.6) * mm, "end": v(-0.55, -740.6) * mm});
            skLineSegment(sketch, "E88.MirrorCS", {"start": v(52.45, -641.22) * mm, "end": v(40.45, -641.22) * mm});
            skLineSegment(sketch, "E89.MirrorCS", {"start": v(-70.55, -740.6) * mm, "end": v(-82.55, -740.6) * mm});
            skLineSegment(sketch, "E90.MirrorCS", {"start": v(72.95, -740.6) * mm, "end": v(60.95, -740.6) * mm});
            skLineSegment(sketch, "E91.MirrorCS", {"start": v(134.45, -641.22) * mm, "end": v(122.45, -641.22) * mm});
            skLineSegment(sketch, "E92.MirrorCS", {"start": v(-50.05, -740.6) * mm, "end": v(-62.05, -740.6) * mm});
            skLineSegment(sketch, "E93.MirrorCS", {"start": v(31.95, -740.6) * mm, "end": v(19.95, -740.6) * mm});
            skLineSegment(sketch, "E94.MirrorCS", {"start": v(-70.55, -641.22) * mm, "end": v(-82.55, -641.22) * mm});
            skLineSegment(sketch, "E95.MirrorCS", {"start": v(-95.25, -748.22) * mm, "end": v(-95.25, -768.22) * mm});
            skLineSegment(sketch, "E96.MirrorCS", {"start": v(-95.25, -748.22) * mm, "end": v(140.8, -748.22) * mm});
            skLineSegment(sketch, "E97.MirrorCS", {"start": v(140.8, -748.22) * mm, "end": v(140.8, -768.22) * mm});
            skLineSegment(sketch, "E98.MirrorCS", {"start": v(134.45, -740.6) * mm, "end": v(134.45, -641.22) * mm});
            skLineSegment(sketch, "E99.MirrorCS", {"start": v(-50.05, -740.6) * mm, "end": v(-50.05, -641.22) * mm});
            skLineSegment(sketch, "E100.MirrorCS", {"start": v(122.45, -740.6) * mm, "end": v(122.45, -641.22) * mm});
            skLineSegment(sketch, "E101.MirrorCS", {"start": v(31.95, -740.6) * mm, "end": v(31.95, -641.22) * mm});
            skLineSegment(sketch, "E102.MirrorCS", {"start": v(-29.55, -740.6) * mm, "end": v(-29.55, -641.22) * mm});
            skLineSegment(sketch, "E103.MirrorCS", {"start": v(52.45, -740.6) * mm, "end": v(52.45, -641.22) * mm});
            skLineSegment(sketch, "E104.MirrorCS", {"start": v(-21.05, -641.22) * mm, "end": v(-21.05, -740.6) * mm});
            skLineSegment(sketch, "E105.MirrorCS", {"start": v(60.95, -740.6) * mm, "end": v(60.95, -641.22) * mm});
            skLineSegment(sketch, "E106.MirrorCS", {"start": v(72.95, -740.6) * mm, "end": v(72.95, -641.22) * mm});
            skLineSegment(sketch, "E107.MirrorCS", {"start": v(140.8, -768.22) * mm, "end": v(-95.25, -768.22) * mm});
            skLineSegment(sketch, "E108.MirrorCS", {"start": v(-70.55, -740.6) * mm, "end": v(-70.55, -641.22) * mm});
            skLineSegment(sketch, "E109.MirrorCS", {"start": v(-41.55, -740.6) * mm, "end": v(-41.55, -641.22) * mm});
            skLineSegment(sketch, "E110.MirrorCS", {"start": v(11.45, -740.6) * mm, "end": v(11.45, -641.22) * mm});
            skLineSegment(sketch, "E111.MirrorCS", {"start": v(40.45, -740.6) * mm, "end": v(40.45, -641.22) * mm});
            skLineSegment(sketch, "E112.MirrorCS", {"start": v(266.7, -817.67) * mm, "end": v(266.7, -624.02) * mm});
            skLineSegment(sketch, "E113.MirrorCS", {"start": v(-266.7, -817.67) * mm, "end": v(-266.7, -624.02) * mm});
            skLineSegment(sketch, "E114.MirrorCS", {"start": v(-9.05, -641.22) * mm, "end": v(-9.05, -740.6) * mm});
            skLineSegment(sketch, "E115.MirrorCS", {"start": v(266.7, -817.67) * mm, "end": v(-266.7, -817.67) * mm});
            skLineSegment(sketch, "E116.MirrorCS", {"start": v(93.45, -740.6) * mm, "end": v(93.45, -641.22) * mm});
            skLineSegment(sketch, "E117.MirrorCS", {"start": v(266.7, -624.02) * mm, "end": v(-266.7, -624.02) * mm});
            skLineSegment(sketch, "E118.MirrorCS", {"start": v(19.95, -740.6) * mm, "end": v(19.95, -641.22) * mm});
            skLineSegment(sketch, "E119.MirrorCS", {"start": v(-62.05, -740.6) * mm, "end": v(-62.05, -641.22) * mm});
            skLineSegment(sketch, "E120.MirrorCS", {"start": v(81.45, -740.6) * mm, "end": v(81.45, -641.22) * mm});
            skLineSegment(sketch, "E121.MirrorCS", {"start": v(-0.55, -740.6) * mm, "end": v(-0.55, -641.22) * mm});
            skLineSegment(sketch, "E122.MirrorCS", {"start": v(101.95, -740.6) * mm, "end": v(101.95, -641.22) * mm});
            skLineSegment(sketch, "E123.MirrorCS", {"start": v(-82.55, -740.6) * mm, "end": v(-82.55, -641.22) * mm});
            skLineSegment(sketch, "E124.MirrorCS", {"start": v(113.95, -740.6) * mm, "end": v(113.95, -641.22) * mm});
            skLineSegment(sketch, "E125.bottom", {"start": v(-247.3, -635.22) * mm, "end": v(-88.55, -635.22) * mm});
            skLineSegment(sketch, "E125.top", {"start": v(-247.3, -679.67) * mm, "end": v(-88.55, -679.67) * mm});
            skLineSegment(sketch, "E125.left", {"start": v(-247.3, -635.22) * mm, "end": v(-247.3, -679.67) * mm});
            skLineSegment(sketch, "E125.right", {"start": v(-88.55, -635.22) * mm, "end": v(-88.55, -679.67) * mm});
            skLineSegment(sketch, "E126.bottom", {"start": v(241.3, -795.85) * mm, "end": v(155.3, -795.85) * mm});
            skLineSegment(sketch, "E126.top", {"start": v(241.3, -645.85) * mm, "end": v(155.3, -645.85) * mm});
            skLineSegment(sketch, "E126.left", {"start": v(241.3, -795.85) * mm, "end": v(241.3, -645.85) * mm});
            skLineSegment(sketch, "E126.right", {"start": v(155.3, -795.85) * mm, "end": v(155.3, -645.85) * mm});
            skPoint(sketch, "E126.middle", {"position": v(198.3, -720.85) * mm});
            skPoint(sketch, "E126.middle.positionSnap0", {"position": v(266.7, -720.85) * mm});
            skPoint(sketch, "E126.centerSnap0", {"position": v(266.7, -720.85) * mm});
            skCircle(sketch, "E127", {"center": v(-167.92, -751.63) * mm, "radius": 44.5 * mm});
            skCircle(sketch, "E128", {"center": v(-209.17, -710.38) * mm, "radius": 2.5 * mm});
            skCircle(sketch, "E129", {"center": v(-126.67, -710.38) * mm, "radius": 2.5 * mm});
            skCircle(sketch, "E130", {"center": v(-209.17, -792.88) * mm, "radius": 2.5 * mm});
            skCircle(sketch, "E131", {"center": v(-126.67, -792.88) * mm, "radius": 2.5 * mm});
            skCircle(sketch, "E132", {"center": v(-216.03, -690.17) * mm, "radius": 2.1 * mm});
            skCircle(sketch, "E133", {"center": v(-119.83, -690.17) * mm, "radius": 2.18 * mm});
            skSolve(sketch);
        }
        {
            var Q0;
            Q0=makeQuery(id+"F16.imprint","IMPRINT",FACE,{"disambiguationData":[TD([[makeQuery(id+"F16.imprint","IMPRINT",EDGE,{"derivedFrom":sQuery(id+"F16.wireOp",EDGE,"eNknI9Zd-MtiG-OOVb-QZow-ef8niGClEtnW.bottom")}),1.0]])]});
            var Q1;
            Q1=makeQuery(id+"F16.imprint","IMPRINT",FACE,{"disambiguationData":[TD([[makeQuery(id+"F16.imprint","IMPRINT",EDGE,{"derivedFrom":sQuery(id+"F16.wireOp",EDGE,"E73.MirrorCS")}),-1.0]])]});
            extrude(context, id + "F17", {"entities" : qUnion([Q0, Q1]), "depth" : 6.38 * mm, "offsetDistance" : 25.4 * mm});
        }
        {
            var Q0;
            Q0=qCreatedBy(makeId("Top.planeOp"),FACE);
            var sketch = newSketch(context, id + "F18", { "sketchPlane" : qUnion([Q0])});
            skPoint(sketch, "E134.0", {"position": v(-279.4, 107.95) * mm});
            skPoint(sketch, "E134.1", {"position": v(279.4, 107.95) * mm});
            skPoint(sketch, "E134.2", {"position": v(-269.88, -95.07) * mm});
            skPoint(sketch, "E134.3", {"position": v(269.88, -95.07) * mm});
            skLineSegment(sketch, "E135.bottom", {"start": v(260.35, 158.75) * mm, "end": v(-260.35, 158.75) * mm});
            skLineSegment(sketch, "E135.top", {"start": v(260.35, 260.35) * mm, "end": v(-260.35, 260.35) * mm});
            skLineSegment(sketch, "E135.left", {"start": v(260.35, 158.75) * mm, "end": v(260.35, 260.35) * mm});
            skLineSegment(sketch, "E135.right", {"start": v(-260.35, 158.75) * mm, "end": v(-260.35, 260.35) * mm});
            skPoint(sketch, "E135.middle", {"position": v(0, 209.55) * mm});
            skLineSegment(sketch, "E136.bottom", {"start": v(263.53, 247.47) * mm, "end": v(-263.53, 247.47) * mm});
            skLineSegment(sketch, "E136.top", {"start": v(263.53, 254) * mm, "end": v(-263.53, 254) * mm});
            skLineSegment(sketch, "E136.left", {"start": v(263.53, 247.47) * mm, "end": v(263.53, 254) * mm});
            skLineSegment(sketch, "E136.right", {"start": v(-263.53, 247.47) * mm, "end": v(-263.53, 254) * mm});
            skPoint(sketch, "E136.middle", {"position": v(0, 250.74) * mm});
            skSolve(sketch);
        }
        {
            var Q0;
            {var subQ0=sQuery(id+"F18.wireOp",EDGE,"E135.bottom");Q0=makeQuery(id+"F18.imprint","IMPRINT",FACE,{"disambiguationData":[TD([[makeQuery(id+"F18.imprint","IMPRINT",EDGE,{"derivedFrom":subQ0}),-1.0]])]});}
            var Q1;
            {var subQ0=sQuery(id+"F18.wireOp",EDGE,"E136.bottom");var subQ1=sQuery(id+"F18.wireOp",EDGE,"E135.left");var subQ2=makeQuery(id+"F18.imprint","INTERSECT",VERTEX,{"derivedFrom":[subQ1,subQ0]});Q1=makeQuery(id+"F18.imprint","IMPRINT",FACE,{"disambiguationData":[TD([[makeQuery(id+"F18.imprint","IMPRINT",EDGE,{"disambiguationData":[TD([[subQ2,-1.0]])],"derivedFrom":subQ1}),1.0]])]});}
            var Q2;
            {var subQ0=sQuery(id+"F18.wireOp",EDGE,"E135.top");Q2=makeQuery(id+"F18.imprint","IMPRINT",FACE,{"disambiguationData":[TD([[makeQuery(id+"F18.imprint","IMPRINT",EDGE,{"derivedFrom":subQ0}),1.0]])]});}
            extrude(context, id + "F19", {"entities" : qUnion([Q0, Q1, Q2]), "oppositeDirection" : true, "depth" : 12.7 * mm, "offsetDistance" : 25.4 * mm});
        }
        {
            var Q0;
            {var subQ0=sQuery(id+"F18.wireOp",EDGE,"E135.top");Q0=makeQuery(id+"F18.imprint","IMPRINT",FACE,{"disambiguationData":[TD([[makeQuery(id+"F18.imprint","IMPRINT",EDGE,{"derivedFrom":subQ0}),1.0]])]});}
            var Q1;
            {var subQ0=sQuery(id+"F18.wireOp",EDGE,"E135.bottom");Q1=makeQuery(id+"F18.imprint","IMPRINT",FACE,{"disambiguationData":[TD([[makeQuery(id+"F18.imprint","IMPRINT",EDGE,{"derivedFrom":subQ0}),-1.0]])]});}
            extrude(context, id + "F20", {"entities" : qUnion([Q0, Q1]), "operationType" : NewBodyOperationType.ADD, "depth" : 6.35 * mm, "offsetDistance" : 25.4 * mm});
        }
        {
            var Q0;
            Q0=qCreatedBy(makeId("Top.planeOp"),FACE);
            var sketch = newSketch(context, id + "F21", { "sketchPlane" : qUnion([Q0])});
            skLineSegment(sketch, "E137.bottom", {"start": v(-237.03, 305.53) * mm, "end": v(245.57, 305.53) * mm});
            skLineSegment(sketch, "E137.top", {"start": v(-237.03, 587.47) * mm, "end": v(245.57, 587.47) * mm});
            skLineSegment(sketch, "E137.left", {"start": v(-249.73, 318.23) * mm, "end": v(-249.73, 574.77) * mm});
            skLineSegment(sketch, "E137.right", {"start": v(258.27, 318.23) * mm, "end": v(258.27, 574.77) * mm});
            skCircle(sketch, "E138", {"center": v(-221.08, 567.15) * mm, "radius": 10 * mm});
            skCircle(sketch, "E139", {"center": v(-221.08, 325.85) * mm, "radius": 10 * mm});
            skCircle(sketch, "E140", {"center": v(229.62, 567.15) * mm, "radius": 10 * mm});
            skCircle(sketch, "E141", {"center": v(229.62, 325.85) * mm, "radius": 10 * mm});
            skPoint(sketch, "E142.visualSharp", {"position": v(-249.73, 587.47) * mm});
            skArc(sketch, "E142.filletArc", {"start": v(-237.03, 587.47) * mm, "mid": v(-246.01, 583.75) * mm, "end": v(-249.73, 574.77) * mm});
            skPoint(sketch, "E143.visualSharp", {"position": v(258.27, 587.47) * mm});
            skArc(sketch, "E143.filletArc", {"start": v(258.27, 574.77) * mm, "mid": v(254.55, 583.75) * mm, "end": v(245.57, 587.47) * mm});
            skPoint(sketch, "E144.visualSharp", {"position": v(-249.73, 305.53) * mm});
            skArc(sketch, "E144.filletArc", {"start": v(-249.73, 318.23) * mm, "mid": v(-246.01, 309.25) * mm, "end": v(-237.03, 305.53) * mm});
            skPoint(sketch, "E145.visualSharp", {"position": v(258.27, 305.53) * mm});
            skArc(sketch, "E145.filletArc", {"start": v(245.57, 305.53) * mm, "mid": v(254.55, 309.25) * mm, "end": v(258.27, 318.23) * mm});
            skPoint(sketch, "E146", {"position": v(-249.73, 446.5) * mm});
            skPoint(sketch, "E147", {"position": v(258.27, 446.5) * mm});
            skPoint(sketch, "E148", {"position": v(4.27, 587.47) * mm});
            skPoint(sketch, "E149", {"position": v(4.27, 305.53) * mm});
            skSolve(sketch);
        }
        {
            var Q0;
            Q0=makeQuery(id+"F21.imprint","IMPRINT",FACE,{"disambiguationData":[TD([[makeQuery(id+"F21.imprint","IMPRINT",EDGE,{"derivedFrom":sQuery(id+"F21.wireOp",EDGE,"E137.bottom")}),1.0]])]});
            extrude(context, id + "F22", {"entities" : qUnion([Q0]), "depth" : 3 * mm, "offsetDistance" : 25.4 * mm});
        }
        {
            var Q0;
            Q0=qCreatedBy(makeId("Top.planeOp"),FACE);
            var sketch = newSketch(context, id + "F23", { "sketchPlane" : qUnion([Q0])});
            skPoint(sketch, "E150.0", {"position": v(-266.7, -817.67) * mm});
            skPoint(sketch, "E150.1", {"position": v(266.7, -817.67) * mm});
            skLineSegment(sketch, "E151.MirrorCS", {"start": v(-95.25, -1002.22) * mm, "end": v(-95.25, -1022.22) * mm});
            skLineSegment(sketch, "E152.MirrorCS", {"start": v(-95.25, -1002.22) * mm, "end": v(140.8, -1002.22) * mm});
            skLineSegment(sketch, "E153.MirrorCS", {"start": v(140.8, -1002.22) * mm, "end": v(140.8, -1022.22) * mm});
            skLineSegment(sketch, "E154.MirrorCS", {"start": v(140.8, -1022.22) * mm, "end": v(-95.25, -1022.22) * mm});
            skLineSegment(sketch, "E155.MirrorCS", {"start": v(266.7, -1071.67) * mm, "end": v(266.7, -878.02) * mm});
            skLineSegment(sketch, "E156.MirrorCS", {"start": v(-266.7, -1071.67) * mm, "end": v(-266.7, -878.02) * mm});
            skLineSegment(sketch, "E157.MirrorCS", {"start": v(266.7, -1071.67) * mm, "end": v(-266.7, -1071.67) * mm});
            skLineSegment(sketch, "E158.MirrorCS", {"start": v(266.7, -878.02) * mm, "end": v(-266.7, -878.02) * mm});
            skLineSegment(sketch, "E159.MirrorCS", {"start": v(-82.55, -994.6) * mm, "end": v(-82.55, -895.22) * mm});
            skLineSegment(sketch, "E160.bottom", {"start": v(-247.3, -889.22) * mm, "end": v(-88.55, -889.22) * mm});
            skLineSegment(sketch, "E160.top", {"start": v(-247.3, -933.67) * mm, "end": v(-88.55, -933.67) * mm});
            skLineSegment(sketch, "E160.left", {"start": v(-247.3, -889.22) * mm, "end": v(-247.3, -933.67) * mm});
            skLineSegment(sketch, "E160.right", {"start": v(-88.55, -889.22) * mm, "end": v(-88.55, -933.67) * mm});
            skLineSegment(sketch, "E161.bottom", {"start": v(241.3, -1049.85) * mm, "end": v(155.3, -1049.85) * mm});
            skLineSegment(sketch, "E161.top", {"start": v(241.3, -899.85) * mm, "end": v(155.3, -899.85) * mm});
            skLineSegment(sketch, "E161.left", {"start": v(241.3, -1049.85) * mm, "end": v(241.3, -899.85) * mm});
            skLineSegment(sketch, "E161.right", {"start": v(155.3, -1049.85) * mm, "end": v(155.3, -899.85) * mm});
            skPoint(sketch, "E161.middle", {"position": v(198.3, -974.85) * mm});
            skPoint(sketch, "E161.middle.positionSnap0", {"position": v(266.7, -974.85) * mm});
            skPoint(sketch, "E161.centerSnap0", {"position": v(266.7, -974.85) * mm});
            skCircle(sketch, "E162", {"center": v(-167.92, -1005.63) * mm, "radius": 44.5 * mm});
            skCircle(sketch, "E163", {"center": v(-209.17, -964.38) * mm, "radius": 2.5 * mm});
            skCircle(sketch, "E164", {"center": v(-126.67, -964.38) * mm, "radius": 2.5 * mm});
            skCircle(sketch, "E165", {"center": v(-209.17, -1046.88) * mm, "radius": 2.5 * mm});
            skCircle(sketch, "E166", {"center": v(-126.67, -1046.88) * mm, "radius": 2.5 * mm});
            skCircle(sketch, "E167", {"center": v(-216.03, -944.17) * mm, "radius": 2.1 * mm});
            skCircle(sketch, "E168", {"center": v(-119.83, -944.17) * mm, "radius": 2.18 * mm});
            skLineSegment(sketch, "E169.bottom", {"start": v(-82.55, -895.22) * mm, "end": v(134.45, -895.22) * mm});
            skLineSegment(sketch, "E169.top", {"start": v(-82.55, -994.6) * mm, "end": v(134.45, -994.6) * mm});
            skLineSegment(sketch, "E169.left", {"start": v(-82.55, -895.22) * mm, "end": v(-82.55, -994.6) * mm});
            skLineSegment(sketch, "E169.right", {"start": v(134.45, -895.22) * mm, "end": v(134.45, -994.6) * mm});
            skSolve(sketch);
        }
        {
            var Q0;
            Q0=makeQuery(id+"F23.imprint","IMPRINT",FACE,{"disambiguationData":[TD([[makeQuery(id+"F23.imprint","IMPRINT",EDGE,{"derivedFrom":sQuery(id+"F23.wireOp",EDGE,"E151.MirrorCS")}),-1.0]])]});
            extrude(context, id + "F24", {"entities" : qUnion([Q0]), "depth" : 6.38 * mm, "offsetDistance" : 25.4 * mm});
        }
        {
            var Q0;
            Q0=qCreatedBy(makeId("Top.planeOp"),FACE);
            var sketch = newSketch(context, id + "F25", { "sketchPlane" : qUnion([Q0])});
            skPoint(sketch, "E170.0", {"position": v(-82.55, -994.6) * mm});
            skPoint(sketch, "E170.1", {"position": v(134.45, -994.6) * mm});
            skLineSegment(sketch, "E171.bottom", {"start": v(-82.55, -1175.91) * mm, "end": v(134.45, -1175.91) * mm});
            skLineSegment(sketch, "E171.top", {"start": v(-82.55, -1275.3) * mm, "end": v(134.45, -1275.3) * mm});
            skLineSegment(sketch, "E171.left", {"start": v(-82.55, -1175.91) * mm, "end": v(-82.55, -1275.3) * mm});
            skLineSegment(sketch, "E171.right", {"start": v(134.45, -1175.91) * mm, "end": v(134.45, -1275.3) * mm});
            skLineSegment(sketch, "E172.bottom", {"start": v(-80.55, -1177.91) * mm, "end": v(132.45, -1177.91) * mm});
            skLineSegment(sketch, "E172.top", {"start": v(-80.55, -1273.3) * mm, "end": v(132.45, -1273.3) * mm});
            skLineSegment(sketch, "E172.left", {"start": v(-80.55, -1177.91) * mm, "end": v(-80.55, -1273.3) * mm});
            skLineSegment(sketch, "E172.right", {"start": v(132.45, -1177.91) * mm, "end": v(132.45, -1273.3) * mm});
            skLineSegment(sketch, "E173", {"start": v(-70.55, -1177.91) * mm, "end": v(-70.55, -1273.3) * mm});
            skLineSegment(sketch, "E174", {"start": v(122.45, -1177.91) * mm, "end": v(122.45, -1273.3) * mm});
            skLineSegment(sketch, "E175", {"start": v(-62.05, -1177.91) * mm, "end": v(-62.05, -1273.3) * mm});
            skLineSegment(sketch, "E176", {"start": v(-50.05, -1177.91) * mm, "end": v(-50.05, -1273.3) * mm});
            skLineSegment(sketch, "E177", {"start": v(113.95, -1177.91) * mm, "end": v(113.95, -1273.3) * mm});
            skLineSegment(sketch, "E178", {"start": v(101.95, -1177.91) * mm, "end": v(101.95, -1273.3) * mm});
            skLineSegment(sketch, "E179", {"start": v(-41.55, -1177.91) * mm, "end": v(-41.55, -1273.3) * mm});
            skLineSegment(sketch, "E180", {"start": v(-29.55, -1177.91) * mm, "end": v(-29.55, -1273.3) * mm});
            skLineSegment(sketch, "E181", {"start": v(-21.05, -1177.91) * mm, "end": v(-21.05, -1273.3) * mm});
            skLineSegment(sketch, "E182", {"start": v(-9.05, -1177.91) * mm, "end": v(-9.05, -1273.3) * mm});
            skLineSegment(sketch, "E183", {"start": v(-0.55, -1177.91) * mm, "end": v(-0.55, -1273.3) * mm});
            skLineSegment(sketch, "E184", {"start": v(11.45, -1273.3) * mm, "end": v(11.45, -1177.91) * mm});
            skLineSegment(sketch, "E185", {"start": v(19.95, -1177.91) * mm, "end": v(19.95, -1273.3) * mm});
            skLineSegment(sketch, "E186", {"start": v(31.95, -1177.91) * mm, "end": v(31.95, -1273.3) * mm});
            skLineSegment(sketch, "E187", {"start": v(40.45, -1177.91) * mm, "end": v(40.45, -1273.3) * mm});
            skLineSegment(sketch, "E188", {"start": v(52.45, -1177.91) * mm, "end": v(52.45, -1273.3) * mm});
            skLineSegment(sketch, "E189", {"start": v(60.95, -1177.91) * mm, "end": v(60.95, -1273.3) * mm});
            skLineSegment(sketch, "E190", {"start": v(72.95, -1177.91) * mm, "end": v(72.95, -1273.3) * mm});
            skLineSegment(sketch, "E191", {"start": v(81.45, -1177.91) * mm, "end": v(81.45, -1273.3) * mm});
            skLineSegment(sketch, "E192", {"start": v(93.45, -1177.91) * mm, "end": v(93.45, -1273.3) * mm});
            skLineSegment(sketch, "E193.bottom", {"start": v(-83.55, -1174.91) * mm, "end": v(135.45, -1174.91) * mm});
            skLineSegment(sketch, "E193.top", {"start": v(-83.55, -1276.3) * mm, "end": v(135.45, -1276.3) * mm});
            skLineSegment(sketch, "E193.left", {"start": v(-83.55, -1174.91) * mm, "end": v(-83.55, -1276.3) * mm});
            skLineSegment(sketch, "E193.right", {"start": v(135.45, -1174.91) * mm, "end": v(135.45, -1276.3) * mm});
            skSolve(sketch);
        }
        {
            var Q0;
            Q0=makeQuery(id+"F25.imprint","IMPRINT",FACE,{"disambiguationData":[TD([[makeQuery(id+"F25.imprint","IMPRINT",EDGE,{"derivedFrom":sQuery(id+"F25.wireOp",EDGE,"E171.bottom")}),-1.0]])]});
            var Q1;
            {var subQ0=sQuery(id+"F25.wireOp",EDGE,"E173");Q1=makeQuery(id+"F25.imprint","IMPRINT",FACE,{"disambiguationData":[TD([[makeQuery(id+"F25.imprint","IMPRINT",EDGE,{"derivedFrom":subQ0}),1.0]])]});}
            var Q2;
            {var subQ0=sQuery(id+"F25.wireOp",EDGE,"E176");Q2=makeQuery(id+"F25.imprint","IMPRINT",FACE,{"disambiguationData":[TD([[makeQuery(id+"F25.imprint","IMPRINT",EDGE,{"derivedFrom":subQ0}),1.0]])]});}
            var Q3;
            {var subQ0=sQuery(id+"F25.wireOp",EDGE,"E180");Q3=makeQuery(id+"F25.imprint","IMPRINT",FACE,{"disambiguationData":[TD([[makeQuery(id+"F25.imprint","IMPRINT",EDGE,{"derivedFrom":subQ0}),1.0]])]});}
            var Q4;
            {var subQ0=sQuery(id+"F25.wireOp",EDGE,"E182");Q4=makeQuery(id+"F25.imprint","IMPRINT",FACE,{"disambiguationData":[TD([[makeQuery(id+"F25.imprint","IMPRINT",EDGE,{"derivedFrom":subQ0}),1.0]])]});}
            var Q5;
            {var subQ0=sQuery(id+"F25.wireOp",EDGE,"E184");Q5=makeQuery(id+"F25.imprint","IMPRINT",FACE,{"disambiguationData":[TD([[makeQuery(id+"F25.imprint","IMPRINT",EDGE,{"derivedFrom":subQ0}),-1.0]])]});}
            var Q6;
            {var subQ0=sQuery(id+"F25.wireOp",EDGE,"E186");Q6=makeQuery(id+"F25.imprint","IMPRINT",FACE,{"disambiguationData":[TD([[makeQuery(id+"F25.imprint","IMPRINT",EDGE,{"derivedFrom":subQ0}),1.0]])]});}
            var Q7;
            {var subQ0=sQuery(id+"F25.wireOp",EDGE,"E188");Q7=makeQuery(id+"F25.imprint","IMPRINT",FACE,{"disambiguationData":[TD([[makeQuery(id+"F25.imprint","IMPRINT",EDGE,{"derivedFrom":subQ0}),1.0]])]});}
            var Q8;
            {var subQ0=sQuery(id+"F25.wireOp",EDGE,"E190");Q8=makeQuery(id+"F25.imprint","IMPRINT",FACE,{"disambiguationData":[TD([[makeQuery(id+"F25.imprint","IMPRINT",EDGE,{"derivedFrom":subQ0}),1.0]])]});}
            var Q9;
            {var subQ0=sQuery(id+"F25.wireOp",EDGE,"E178");Q9=makeQuery(id+"F25.imprint","IMPRINT",FACE,{"disambiguationData":[TD([[makeQuery(id+"F25.imprint","IMPRINT",EDGE,{"derivedFrom":subQ0}),-1.0]])]});}
            var Q10;
            {var subQ0=sQuery(id+"F25.wireOp",EDGE,"E174");Q10=makeQuery(id+"F25.imprint","IMPRINT",FACE,{"disambiguationData":[TD([[makeQuery(id+"F25.imprint","IMPRINT",EDGE,{"derivedFrom":subQ0}),-1.0]])]});}
            var Q11;
            Q11=makeQuery(id+"F25.imprint","IMPRINT",FACE,{"disambiguationData":[TD([[makeQuery(id+"F25.imprint","IMPRINT",EDGE,{"derivedFrom":sQuery(id+"F25.wireOp",EDGE,"E171.bottom")}),1.0]])]});
            extrude(context, id + "F26", {"entities" : qUnion([Q0, Q1, Q2, Q3, Q4, Q5, Q6, Q7, Q8, Q9, Q10, Q11]), "depth" : 3 * mm, "offsetDistance" : 25.4 * mm});
        }
        {
            var Q0;
            Q0=makeQuery(id+"F25.imprint","IMPRINT",FACE,{"disambiguationData":[TD([[makeQuery(id+"F25.imprint","IMPRINT",EDGE,{"derivedFrom":sQuery(id+"F25.wireOp",EDGE,"E171.bottom")}),-1.0]])]});
            extrude(context, id + "F27", {"entities" : qUnion([Q0]), "operationType" : NewBodyOperationType.ADD, "depth" : 9.4 * mm, "offsetDistance" : 25.4 * mm});
        }
    });
